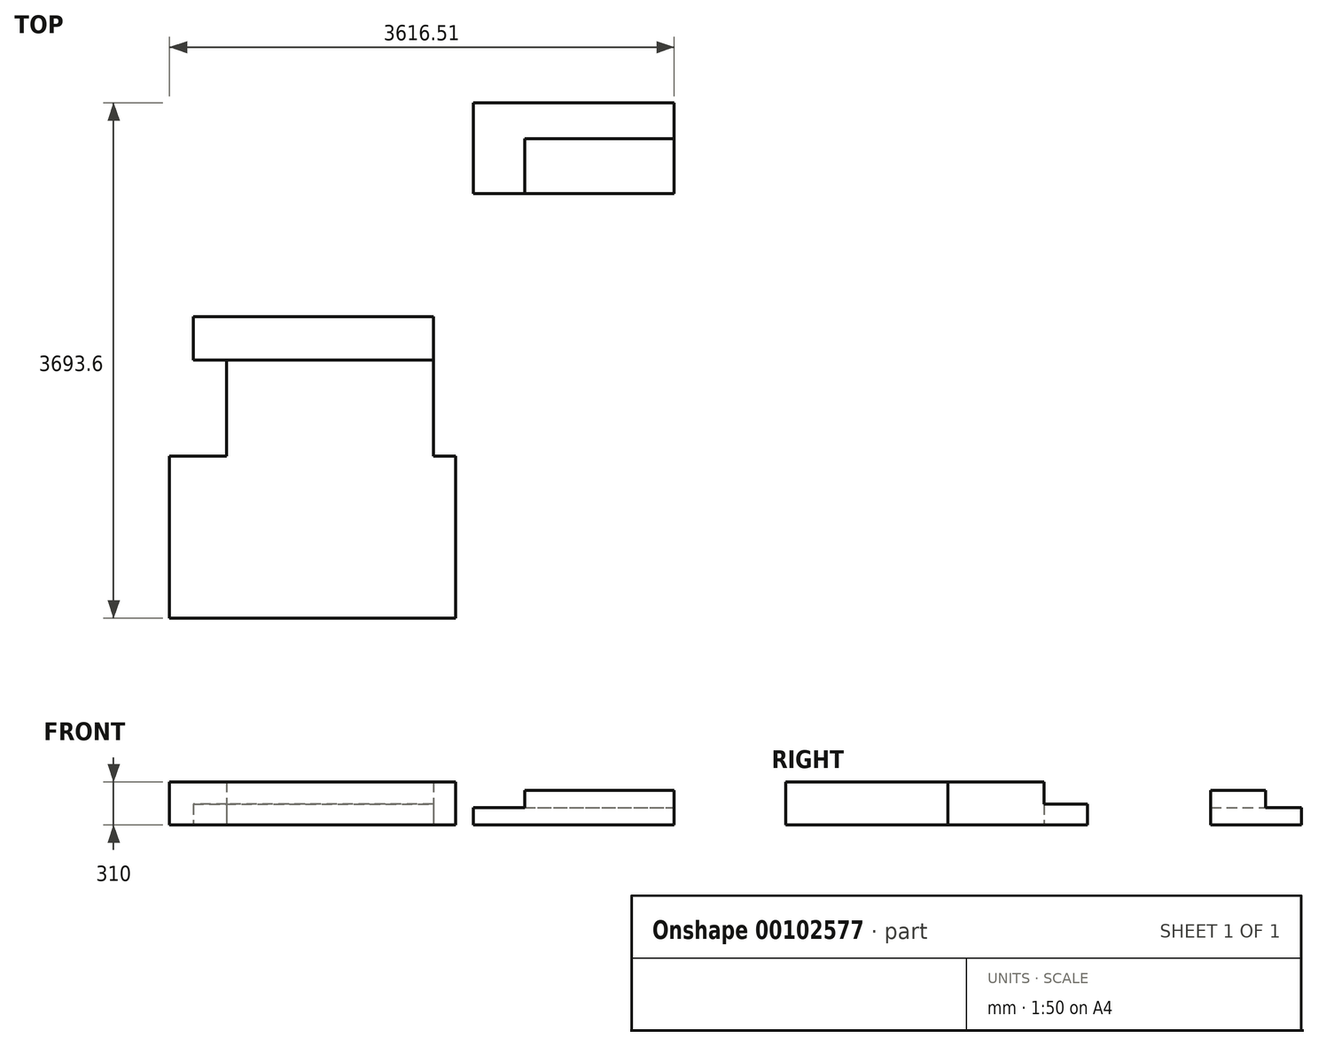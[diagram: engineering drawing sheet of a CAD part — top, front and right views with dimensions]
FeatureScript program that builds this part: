
annotation { "Feature Type Name" : "Feature", "Feature Type Description" : "" }
export const myFeature = defineFeature(function(context is Context, id is Id, definition is map)
    precondition{}
    {
        {
            var Q0;
            Q0=qCreatedBy(makeId("Top.planeOp"),FACE);
            var sketch = newSketch(context, id + "F0", { "sketchPlane" : qUnion([Q0])});
            skLineSegment(sketch, "E0", {"start": v(-63.49, 22.15) * mm, "end": v(2176.51, 22.15) * mm});
            skLineSegment(sketch, "E1", {"start": v(2176.51, 22.15) * mm, "end": v(2176.51, 672.15) * mm});
            skLineSegment(sketch, "E2", {"start": v(2176.51, 672.15) * mm, "end": v(3616.51, 672.15) * mm});
            skLineSegment(sketch, "E3", {"start": v(3616.51, 672.15) * mm, "end": v(3616.51, 1592.15) * mm});
            skLineSegment(sketch, "E4", {"start": v(3616.51, 1592.15) * mm, "end": v(3946.51, 1592.15) * mm});
            skLineSegment(sketch, "E5", {"start": v(3946.51, 1592.15) * mm, "end": v(3946.51, 3002.15) * mm});
            skLineSegment(sketch, "E6", {"start": v(3946.51, 3002.15) * mm, "end": v(4946.51, 3002.15) * mm});
            skLineSegment(sketch, "E7", {"start": v(4946.51, 3002.15) * mm, "end": v(4946.51, 3422.15) * mm});
            skLineSegment(sketch, "E8", {"start": v(4946.51, 3422.15) * mm, "end": v(-63.49, 3422.15) * mm});
            skLineSegment(sketch, "E9", {"start": v(-63.49, 3422.15) * mm, "end": v(-63.49, 22.15) * mm});
            skSolve(sketch);
        }
        {
            var Q0;
            Q0=makeQuery(id+"F0.imprint","IMPRINT",FACE,{"disambiguationData":[TD([[makeQuery(id+"F0.imprint","IMPRINT",EDGE,{"derivedFrom":sQuery(id+"F0.wireOp",EDGE,"E0")}),1.0]])]});
            var sketch = newSketch(context, id + "F1", { "sketchPlane" : qUnion([Q0])});
            skLineSegment(sketch, "E10.bottom", {"start": v(2546.51, 417.15) * mm, "end": v(3616.51, 417.15) * mm});
            skLineSegment(sketch, "E10.top", {"start": v(2546.51, 22.15) * mm, "end": v(3616.51, 22.15) * mm});
            skLineSegment(sketch, "E10.left", {"start": v(2546.51, 417.15) * mm, "end": v(2546.51, 22.15) * mm});
            skLineSegment(sketch, "E10.right", {"start": v(3616.51, 417.15) * mm, "end": v(3616.51, 22.15) * mm});
            skSolve(sketch);
        }
        {
            var Q0;
            Q0=makeQuery(id+"F1.imprint","IMPRINT",FACE,{"disambiguationData":[TD([[makeQuery(id+"F1.imprint","IMPRINT",EDGE,{"derivedFrom":sQuery(id+"F1.wireOp",EDGE,"E10.bottom")}),-1.0]])]});
            extrude(context, id + "F2", {"entities" : qUnion([Q0]), "depth" : 250 * mm, "offsetDistance" : 25 * mm});
        }
        {
            var Q0;
            Q0=makeQuery(id+"F0.imprint","IMPRINT",FACE,{"disambiguationData":[TD([[makeQuery(id+"F0.imprint","IMPRINT",EDGE,{"derivedFrom":sQuery(id+"F0.wireOp",EDGE,"E0")}),1.0]])]});
            var sketch = newSketch(context, id + "F3", { "sketchPlane" : qUnion([Q0])});
            skLineSegment(sketch, "E11", {"start": v(2176.51, 22.15) * mm, "end": v(2546.51, 22.15) * mm});
            skLineSegment(sketch, "E12", {"start": v(2546.51, 22.15) * mm, "end": v(2546.51, 417.15) * mm});
            skLineSegment(sketch, "E13", {"start": v(2546.51, 417.15) * mm, "end": v(3616.51, 417.15) * mm});
            skLineSegment(sketch, "E14", {"start": v(3616.51, 417.15) * mm, "end": v(3616.51, 672.15) * mm});
            skLineSegment(sketch, "E15", {"start": v(3616.51, 672.15) * mm, "end": v(2176.51, 672.15) * mm});
            skLineSegment(sketch, "E16", {"start": v(2176.51, 22.15) * mm, "end": v(2176.51, 672.15) * mm});
            skSolve(sketch);
        }
        {
            var Q0;
            Q0=makeQuery(id+"F3.imprint","IMPRINT",FACE,{"disambiguationData":[TD([[makeQuery(id+"F3.imprint","IMPRINT",EDGE,{"derivedFrom":sQuery(id+"F3.wireOp",EDGE,"E11")}),1.0]])]});
            extrude(context, id + "F4", {"entities" : qUnion([Q0]), "operationType" : NewBodyOperationType.ADD, "depth" : 125 * mm, "offsetDistance" : 25 * mm});
        }
        {
            var Q0;
            Q0=makeQuery(id+"F0.imprint","IMPRINT",FACE,{"disambiguationData":[TD([[makeQuery(id+"F0.imprint","IMPRINT",EDGE,{"derivedFrom":sQuery(id+"F0.wireOp",EDGE,"E0")}),1.0]])]});
            var sketch = newSketch(context, id + "F5", { "sketchPlane" : qUnion([Q0])});
            skLineSegment(sketch, "E17", {"start": v(1890, -1861.45) * mm, "end": v(2050, -1861.45) * mm});
            skLineSegment(sketch, "E18", {"start": v(2050, -1861.45) * mm, "end": v(2050, -3021.45) * mm});
            skLineSegment(sketch, "E19", {"start": v(2050, -3021.45) * mm, "end": v(0, -3021.45) * mm});
            skLineSegment(sketch, "E20", {"start": v(0, -3021.45) * mm, "end": v(0, -1861.45) * mm});
            skLineSegment(sketch, "E21", {"start": v(0, -1861.45) * mm, "end": v(410, -1861.45) * mm});
            skLineSegment(sketch, "E22", {"start": v(410, -1861.45) * mm, "end": v(410, -1171.45) * mm});
            skLineSegment(sketch, "E23", {"start": v(410, -1171.45) * mm, "end": v(1890, -1171.45) * mm});
            skLineSegment(sketch, "E24", {"start": v(1890, -1861.45) * mm, "end": v(1890, -1171.45) * mm});
            skSolve(sketch);
        }
        {
            var Q0;
            Q0=makeQuery(id+"F5.imprint","IMPRINT",FACE,{"disambiguationData":[TD([[makeQuery(id+"F5.imprint","IMPRINT",EDGE,{"derivedFrom":sQuery(id+"F5.wireOp",EDGE,"E17")}),-1.0]])]});
            var sketch = newSketch(context, id + "F6", { "sketchPlane" : qUnion([Q0])});
            skLineSegment(sketch, "E25", {"start": v(1890, -861.45) * mm, "end": v(1890, -1171.45) * mm});
            skLineSegment(sketch, "E26", {"start": v(1890, -1171.45) * mm, "end": v(170, -1171.45) * mm});
            skLineSegment(sketch, "E27", {"start": v(170, -1171.45) * mm, "end": v(170, -861.45) * mm});
            skLineSegment(sketch, "E28", {"start": v(170, -861.45) * mm, "end": v(1890, -861.45) * mm});
            skSolve(sketch);
        }
        {
            var Q0;
            Q0=makeQuery(id+"F5.imprint","IMPRINT",FACE,{"disambiguationData":[TD([[makeQuery(id+"F5.imprint","IMPRINT",EDGE,{"derivedFrom":sQuery(id+"F5.wireOp",EDGE,"E17")}),-1.0]])]});
            extrude(context, id + "F7", {"entities" : qUnion([Q0]), "depth" : 310 * mm, "offsetDistance" : 25 * mm});
        }
        {
            var Q0;
            {var subQ3=sQuery(id+"F6.wireOp",EDGE,"E25");Q0=makeQuery(id+"F6.imprint","IMPRINT",FACE,{"disambiguationData":[TD([[makeQuery(id+"F6.imprint","IMPRINT",EDGE,{"derivedFrom":subQ3}),-1.0]])]});}
            extrude(context, id + "F8", {"entities" : qUnion([Q0]), "operationType" : NewBodyOperationType.ADD, "depth" : 150 * mm, "offsetDistance" : 25 * mm});
        }
    });
